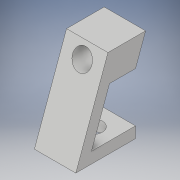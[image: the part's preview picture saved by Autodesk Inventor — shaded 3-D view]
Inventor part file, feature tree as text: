
AUTODESK INVENTOR PART (.ipt)
format: ipt  version: 2019 (Build 230136000, 136)  size: 300,544 bytes
history: native  units: in
note: dims shown in document units (in); Inventor stores cm internally (conversion verified against a paired STEP export)
features: extrude x7, sketch x7, projected_geometry x1
ambient origin geometry x8: Origin, YZ Plane, XZ Plane, XY Plane, X Axis, Y Axis, Z Axis, Center Point
bodies: Solid1 (feature_tree)
feature tree (15):
  extrude  "Extrusion1"  Depth=0.2953in TaperAngle=0.0deg
  extrude  "Extrusion2"  Depth=0.1575in
  extrude  "Extrusion5"  Depth=0.3937in
  extrude  "Extrusion6"  Depth=0.186in
  extrude  "Extrusion4"  Depth=0.3937in
  extrude  "Extrusion7"  Depth=0.3937in
  extrude  "Extrusion3"  Depth=0.3937in TaperAngle=0.0deg
  sketch  "Sketch1"  dims[d12=0.481in d14=0.2953in d15=0.0in]
  sketch  "Sketch2"  dims[d17=0.5906in d18=0.1575in]
  sketch  "Sketch3"  dims[d23=0.315in d24=0.3937in]
  sketch  "Sketch4"  dims[d25=0.481in d26=0.186in]
  sketch  "Sketch5"  dims[d27=0.3937in d28=0.0in d29=0.1378in]
  projected_geometry  "Projected Loop1"
  sketch  "Sketch6"  dims[d30=0.3937in d31=0.0in d32=0.1378in]
  sketch  "Sketch7"  dims[d33=0.3937in d34=0.0in d37=0.3937in d38=0.0in d39=0.1969in d40=0.0in d41=0.0394in d42=0.481in d43=0.3937in d44=0.0in d45=0.0394in d46=0.0394in d47=0.3937in d48=0.0in]
